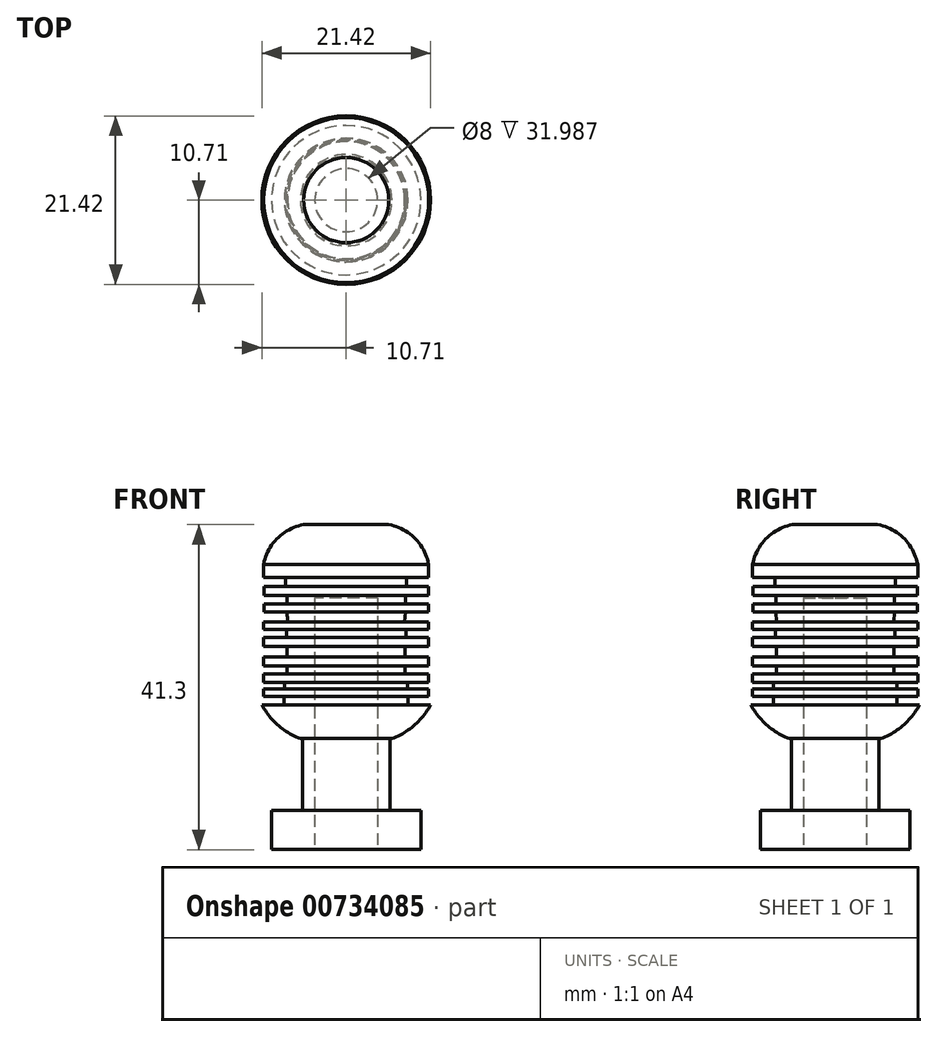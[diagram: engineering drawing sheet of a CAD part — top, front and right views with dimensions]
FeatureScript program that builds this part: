
annotation { "Feature Type Name" : "Feature", "Feature Type Description" : "" }
export const myFeature = defineFeature(function(context is Context, id is Id, definition is map)
    precondition{}
    {
        {
            var Q0;
            Q0=qCreatedBy(makeId("Top.planeOp"),FACE);
            var sketch = newSketch(context, id + "F0", { "sketchPlane" : qUnion([Q0])});
            skCircle(sketch, "E0", {"center": v(0, 0) * mm, "radius": 4 * mm});
            skSolve(sketch);
        }
        {
            var Q0;
            Q0 = qSketchRegion(id + "F2", true);
            var Q1;
            Q1=makeQuery(id+"F0.imprint","IMPRINT",FACE,{"disambiguationData":[TD([[makeQuery(id+"F0.imprint","IMPRINT",EDGE,{"derivedFrom":sQuery(id+"F0.wireOp",EDGE,"E0")}),1.0]])]});
            extrude(context, id + "F1", {"entities" : qUnion([Q0, Q1]), "depth" : 135 * mm, "offsetDistance" : 25 * mm});
        }
        {
            var Q0;
            Q0=qCreatedBy(makeId("Front.planeOp"),FACE);
            var sketch = newSketch(context, id + "F2", { "sketchPlane" : qUnion([Q0])});
            skLineSegment(sketch, "E1", {"start": v(-10.48, 139.27) * mm, "end": v(-10.48, 137.58) * mm});
            skLineSegment(sketch, "E2", {"start": v(-5.81, 117.13) * mm, "end": v(-5.57, 117.13) * mm});
            skLineSegment(sketch, "E3", {"start": v(-5.57, 117.13) * mm, "end": v(-5.57, 107.97) * mm});
            skLineSegment(sketch, "E4", {"start": v(-5.57, 107.97) * mm, "end": v(-9.48, 107.97) * mm});
            skLineSegment(sketch, "E5", {"start": v(-9.48, 107.97) * mm, "end": v(-9.48, 103.01) * mm});
            skLineSegment(sketch, "E6", {"start": v(-9.48, 103.01) * mm, "end": v(0, 103.01) * mm});
            skArc(sketch, "E7", {"start": v(-5.4, 144.3) * mm, "mid": v(-8.72, 142.57) * mm, "end": v(-10.48, 139.27) * mm});
            skPoint(sketch, "E8.orphan", {"position": v(8.6, 144.32) * mm});
            skArc(sketch, "E9", {"start": v(-10.71, 121.42) * mm, "mid": v(-8.66, 118.82) * mm, "end": v(-5.81, 117.13) * mm});
            skPoint(sketch, "E10.orphan", {"position": v(-10.48, 117.13) * mm});
            skPoint(sketch, "E11.orphan", {"position": v(8.6, 117.13) * mm});
            skLineSegment(sketch, "E12", {"start": v(0, 103.01) * mm, "end": v(0, 144.31) * mm});
            skPoint(sketch, "E12.startSnap0", {"position": v(0, 96.2) * mm});
            skLineSegment(sketch, "E13.trimOffspring", {"start": v(0, 144.31) * mm, "end": v(-5.4, 144.3) * mm});
            skPoint(sketch, "E14.start.orphan", {"position": v(8.6, 138.79) * mm});
            skPoint(sketch, "E15.orphan", {"position": v(4.15, 117.13) * mm});
            skPoint(sketch, "E16.end.orphan", {"position": v(8.6, 107.97) * mm});
            skPoint(sketch, "E17.orphan", {"position": v(8.6, 103.01) * mm});
            skPoint(sketch, "E18.center.orphan", {"position": v(3.65, 138.79) * mm});
            skPoint(sketch, "E19.end.orphan", {"position": v(1.6, 144.31) * mm});
            skPoint(sketch, "E20.orphan", {"position": v(0, 101.22) * mm});
            skLineSegment(sketch, "E21", {"start": v(-10.48, 137.58) * mm, "end": v(-7.68, 137.58) * mm});
            skLineSegment(sketch, "E22", {"start": v(-7.52, 135.32) * mm, "end": v(-7.52, 135.32) * mm});
            skLineSegment(sketch, "E23", {"start": v(-7.44, 131.93) * mm, "end": v(-10.48, 131.93) * mm});
            skLineSegment(sketch, "E24", {"start": v(-10.48, 130.98) * mm, "end": v(-7.58, 130.98) * mm});
            skLineSegment(sketch, "E25", {"start": v(-7.58, 130.98) * mm, "end": v(-7.58, 129.95) * mm});
            skLineSegment(sketch, "E26", {"start": v(-7.58, 129.95) * mm, "end": v(-10.48, 129.95) * mm});
            skLineSegment(sketch, "E27", {"start": v(-10.48, 128.84) * mm, "end": v(-7.49, 128.84) * mm});
            skLineSegment(sketch, "E28", {"start": v(-7.49, 128.84) * mm, "end": v(-7.49, 127.48) * mm});
            skLineSegment(sketch, "E29", {"start": v(-7.49, 127.48) * mm, "end": v(-10.48, 127.48) * mm});
            skLineSegment(sketch, "E30", {"start": v(-10.48, 126.33) * mm, "end": v(-7.49, 126.33) * mm});
            skLineSegment(sketch, "E31", {"start": v(-7.49, 126.33) * mm, "end": v(-7.49, 125.3) * mm});
            skLineSegment(sketch, "E32", {"start": v(-7.49, 125.3) * mm, "end": v(-10.48, 125.3) * mm});
            skLineSegment(sketch, "E33", {"start": v(-7.86, 121.42) * mm, "end": v(-10.71, 121.42) * mm});
            skPoint(sketch, "E34.start.orphan", {"position": v(-12.85, 122.87) * mm});
            skPoint(sketch, "E35.start.orphan", {"position": v(-8.97, 132.8) * mm});
            skLineSegment(sketch, "E36", {"start": v(-7.52, 134.22) * mm, "end": v(-10.45, 134.22) * mm});
            skLineSegment(sketch, "E37", {"start": v(-10.45, 134.22) * mm, "end": v(-10.45, 133.23) * mm});
            skLineSegment(sketch, "E38", {"start": v(-10.45, 133.23) * mm, "end": v(-7.52, 133.23) * mm});
            skLineSegment(sketch, "E39", {"start": v(-7.52, 133.23) * mm, "end": v(-7.44, 131.93) * mm});
            skLineSegment(sketch, "E40", {"start": v(-10.48, 124.24) * mm, "end": v(-7.82, 124.24) * mm});
            skLineSegment(sketch, "E41", {"start": v(-7.82, 124.24) * mm, "end": v(-7.82, 123.45) * mm});
            skLineSegment(sketch, "E42", {"start": v(-7.82, 123.45) * mm, "end": v(-10.48, 123.45) * mm});
            skPoint(sketch, "E43.orphan", {"position": v(-11.78, 122.43) * mm});
            skLineSegment(sketch, "E44", {"start": v(-10.48, 122.48) * mm, "end": v(-7.86, 122.48) * mm});
            skLineSegment(sketch, "E45", {"start": v(-7.86, 122.48) * mm, "end": v(-7.86, 121.42) * mm});
            skPoint(sketch, "E46.end.orphan", {"position": v(-8.97, 135.32) * mm});
            skLineSegment(sketch, "E47", {"start": v(-10.48, 136.48) * mm, "end": v(-7.68, 136.48) * mm});
            skLineSegment(sketch, "E48", {"start": v(-7.68, 136.48) * mm, "end": v(-10.45, 136.48) * mm});
            skPoint(sketch, "E49.end.orphan", {"position": v(-7.68, 137.58) * mm});
            skPoint(sketch, "E50.orphan", {"position": v(-7.46, 137.58) * mm});
            skLineSegment(sketch, "E51", {"start": v(-7.68, 136.48) * mm, "end": v(-7.68, 137.58) * mm});
            skLineSegment(sketch, "E52", {"start": v(-10.45, 136.48) * mm, "end": v(-10.45, 135.3) * mm});
            skLineSegment(sketch, "E53", {"start": v(-10.45, 135.3) * mm, "end": v(-7.52, 135.32) * mm});
            skLineSegment(sketch, "E54", {"start": v(-7.52, 134.22) * mm, "end": v(-7.52, 135.32) * mm});
            skLineSegment(sketch, "E55", {"start": v(-10.48, 137.58) * mm, "end": v(-10.48, 136.48) * mm});
            skLineSegment(sketch, "E56.trimOffspring", {"start": v(-10.48, 131.93) * mm, "end": v(-10.48, 130.98) * mm});
            skLineSegment(sketch, "E57.trimOffspring", {"start": v(-10.48, 129.95) * mm, "end": v(-10.48, 128.84) * mm});
            skLineSegment(sketch, "E58.trimOffspring", {"start": v(-10.48, 127.48) * mm, "end": v(-10.48, 126.33) * mm});
            skLineSegment(sketch, "E59.trimOffspring", {"start": v(-10.48, 125.3) * mm, "end": v(-10.48, 124.24) * mm});
            skLineSegment(sketch, "E60.trimOffspring", {"start": v(-10.48, 123.45) * mm, "end": v(-10.48, 122.48) * mm});
            skPoint(sketch, "E61.orphan", {"position": v(-12.85, 123.45) * mm});
            skSolve(sketch);
        }
        {
            var Q0;
            Q0=makeQuery(id+"F2.imprint","IMPRINT",FACE,{"disambiguationData":[TD([[makeQuery(id+"F2.imprint","IMPRINT",EDGE,{"derivedFrom":sQuery(id+"F2.wireOp",EDGE,"E1")}),1.0]])]});
            var Q1;
            Q1=sQuery(id+"F2.wireOp",EDGE,"E12");
            revolve(context, id + "F3", {"surfaceOperationType" : NewSurfaceOperationType.NEW, "entities" : qUnion([Q0]), "axis" : qUnion([Q1]), "revolveType" : RevolveType.FULL});
        }
        {
            var Q0;
            Q0=makeQuery(id+"F1.opExtrude","SWEPT_BODY",BODY,{"disambiguationData":[OSD([sQuery(id+"F0.wireOp",EDGE,"E0")])]});
            var Q1;
            Q1=makeQuery(id+"F3.opRevolve","SWEPT_BODY",BODY,{"disambiguationData":[OSD([sQuery(id+"F2.wireOp",EDGE,"E1"),sQuery(id+"F2.wireOp",EDGE,"E2"),sQuery(id+"F2.wireOp",EDGE,"E3"),sQuery(id+"F2.wireOp",EDGE,"E4"),sQuery(id+"F2.wireOp",EDGE,"E5"),sQuery(id+"F2.wireOp",EDGE,"E6"),sQuery(id+"F2.wireOp",EDGE,"E7"),sQuery(id+"F2.wireOp",EDGE,"E9"),sQuery(id+"F2.wireOp",EDGE,"E12"),sQuery(id+"F2.wireOp",EDGE,"E13.trimOffspring"),sQuery(id+"F2.wireOp",EDGE,"E21"),sQuery(id+"F2.wireOp",EDGE,"E23"),sQuery(id+"F2.wireOp",EDGE,"E24"),sQuery(id+"F2.wireOp",EDGE,"E25"),sQuery(id+"F2.wireOp",EDGE,"E26"),sQuery(id+"F2.wireOp",EDGE,"E27"),sQuery(id+"F2.wireOp",EDGE,"E28"),sQuery(id+"F2.wireOp",EDGE,"E29"),sQuery(id+"F2.wireOp",EDGE,"E30"),sQuery(id+"F2.wireOp",EDGE,"E31"),sQuery(id+"F2.wireOp",EDGE,"E32"),sQuery(id+"F2.wireOp",EDGE,"E33"),sQuery(id+"F2.wireOp",EDGE,"E36"),sQuery(id+"F2.wireOp",EDGE,"E37"),sQuery(id+"F2.wireOp",EDGE,"E38"),sQuery(id+"F2.wireOp",EDGE,"E39"),sQuery(id+"F2.wireOp",EDGE,"E40"),sQuery(id+"F2.wireOp",EDGE,"E41"),sQuery(id+"F2.wireOp",EDGE,"E42"),sQuery(id+"F2.wireOp",EDGE,"E44"),sQuery(id+"F2.wireOp",EDGE,"E45"),sQuery(id+"F2.wireOp",EDGE,"E48"),sQuery(id+"F2.wireOp",EDGE,"E51"),sQuery(id+"F2.wireOp",EDGE,"E52"),sQuery(id+"F2.wireOp",EDGE,"E53"),sQuery(id+"F2.wireOp",EDGE,"E54"),sQuery(id+"F2.wireOp",EDGE,"E56.trimOffspring"),sQuery(id+"F2.wireOp",EDGE,"E57.trimOffspring"),sQuery(id+"F2.wireOp",EDGE,"E58.trimOffspring"),sQuery(id+"F2.wireOp",EDGE,"E59.trimOffspring"),sQuery(id+"F2.wireOp",EDGE,"E60.trimOffspring")])]});
            booleanBodies(context, id + "F4", {"operationType" : BooleanOperationType.SUBTRACTION, "tools" : qUnion([Q0]), "targets" : qUnion([Q1])});
        }
    });
